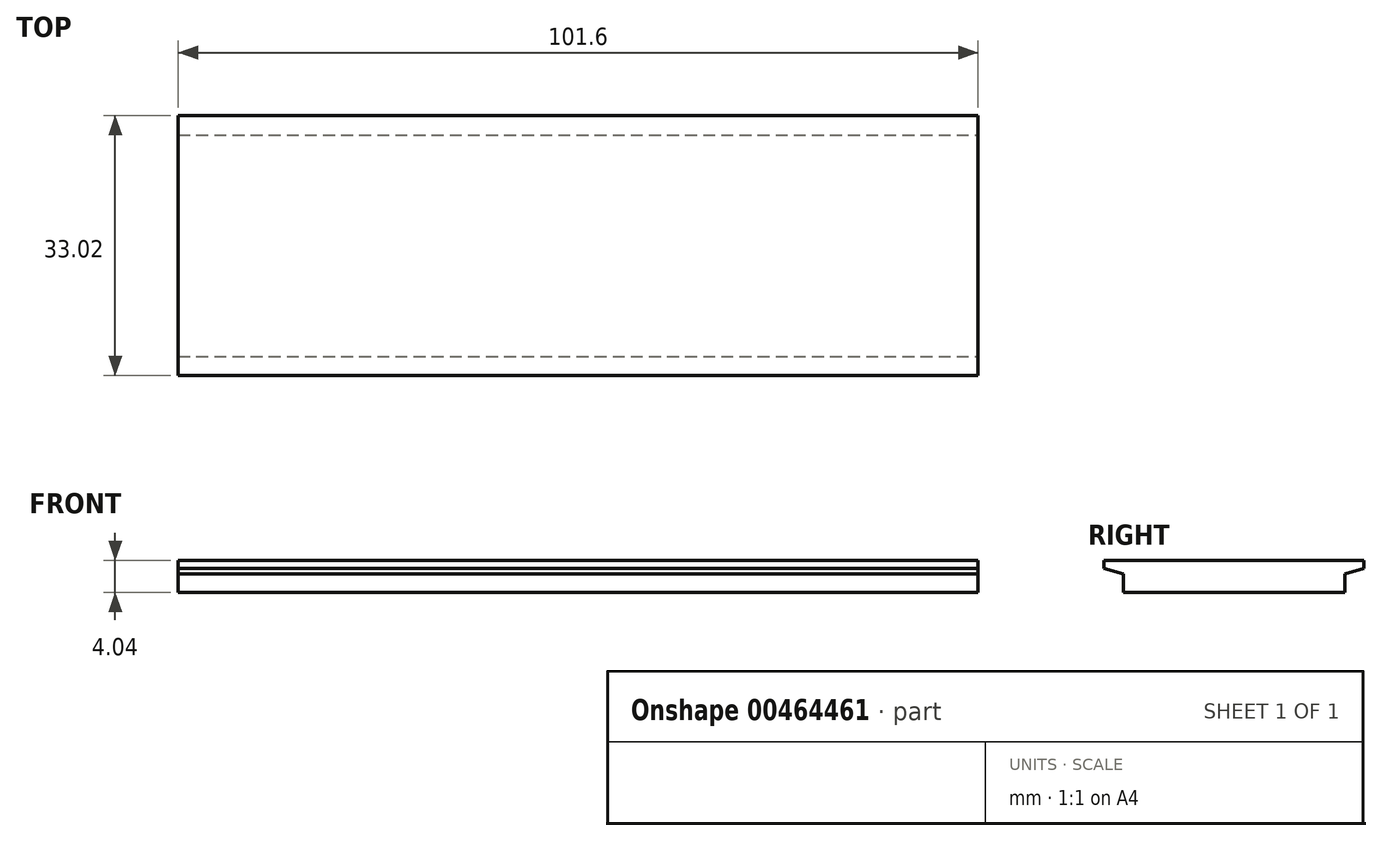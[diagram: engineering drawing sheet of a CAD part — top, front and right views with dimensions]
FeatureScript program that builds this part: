
annotation { "Feature Type Name" : "Feature", "Feature Type Description" : "" }
export const myFeature = defineFeature(function(context is Context, id is Id, definition is map)
    precondition{}
    {
        {
            var Q0;
            Q0=qCreatedBy(makeId("Top.planeOp"),FACE);
            var sketch = newSketch(context, id + "F0", { "sketchPlane" : qUnion([Q0])});
            skLineSegment(sketch, "E0", {"start": v(-50.8, 16.51) * mm, "end": v(50.8, 16.51) * mm});
            skLineSegment(sketch, "E1", {"start": v(50.8, 16.51) * mm, "end": v(50.8, -16.51) * mm});
            skLineSegment(sketch, "E2", {"start": v(50.8, -16.51) * mm, "end": v(-50.8, -16.51) * mm});
            skLineSegment(sketch, "E3", {"start": v(-50.8, -16.51) * mm, "end": v(-50.8, 16.51) * mm});
            skSolve(sketch);
        }
        {
            var Q0;
            Q0=makeQuery(id+"F0.imprint","IMPRINT",FACE,{"disambiguationData":[TD([[makeQuery(id+"F0.imprint","IMPRINT",EDGE,{"derivedFrom":sQuery(id+"F0.wireOp",EDGE,"E0")}),-1.0]])]});
            extrude(context, id + "F1", {"entities" : qUnion([Q0]), "depth" : 4.04 * mm});
        }
        {
            var Q0;
            Q0=makeQuery(id+"F1.opExtrude","SWEPT_FACE",FACE,{"disambiguationData":[OSD([sQuery(id+"F0.wireOp",EDGE,"E1")])]});
            var sketch = newSketch(context, id + "F2", { "sketchPlane" : qUnion([Q0])});
            skLineSegment(sketch, "E4", {"start": v(16.51, 3.02) * mm, "end": v(14.07, 2.33) * mm});
            skLineSegment(sketch, "E5", {"start": v(14.07, 2.33) * mm, "end": v(14.07, 0) * mm});
            skLineSegment(sketch, "E6", {"start": v(16.51, 4.04) * mm, "end": v(16.51, 3.02) * mm});
            skLineSegment(sketch, "E7", {"start": v(0, 0) * mm, "end": v(0, 10.7) * mm, "construction": true});
            skPoint(sketch, "E7.endSnap0", {"position": v(0, 4.04) * mm});
            skLineSegment(sketch, "E8.MirrorCS", {"start": v(-16.51, 4.04) * mm, "end": v(-16.51, 3.02) * mm});
            skLineSegment(sketch, "E9.MirrorCS", {"start": v(-16.51, 3.02) * mm, "end": v(-14.07, 2.33) * mm});
            skLineSegment(sketch, "E10.MirrorCS", {"start": v(-14.07, 2.33) * mm, "end": v(-14.07, 0) * mm});
            skSolve(sketch);
        }
        {
            var Q0;
            {var subQ0=sQuery(id+"F2.wireOp",EDGE,"E9.MirrorCS");Q0=makeQuery(id+"F2.imprint","IMPRINT",FACE,{"disambiguationData":[TD([[makeQuery(id+"F2.imprint","IMPRINT",EDGE,{"derivedFrom":subQ0}),-1.0]])]});}
            var Q1;
            {var subQ0=sQuery(id+"F2.wireOp",EDGE,"E4");Q1=makeQuery(id+"F2.imprint","IMPRINT",FACE,{"disambiguationData":[TD([[makeQuery(id+"F2.imprint","IMPRINT",EDGE,{"derivedFrom":subQ0}),1.0]])]});}
            extrude(context, id + "F3", {"entities" : qUnion([Q0, Q1]), "operationType" : NewBodyOperationType.REMOVE, "oppositeDirection" : true, "depth" : 76.2 * mm});
        }
        {
            var Q0;
            Q0=makeQuery(id+"F3.boolean.opBoolean","COPY",FACE,{"derivedFrom":makeQuery(id+"F3.opExtrude","CAP_FACE",FACE,{"disambiguationData":[OSD([sQuery(id+"F0.wireOp",EDGE,"E1"),sQuery(id+"F0.wireOp",EDGE,"E2"),sQuery(id+"F2.wireOp",EDGE,"E9.MirrorCS"),sQuery(id+"F2.wireOp",EDGE,"E10.MirrorCS")])],"isStart":false})});
            extrude(context, id + "F4", {"entities" : qUnion([Q0]), "operationType" : NewBodyOperationType.REMOVE, "oppositeDirection" : true, "depth" : 38.1 * mm});
        }
        {
            var Q0;
            Q0=makeQuery(id+"F3.boolean.opBoolean","COPY",FACE,{"derivedFrom":makeQuery(id+"F3.opExtrude","CAP_FACE",FACE,{"disambiguationData":[OSD([sQuery(id+"F0.wireOp",EDGE,"E0"),sQuery(id+"F0.wireOp",EDGE,"E1"),sQuery(id+"F2.wireOp",EDGE,"E4"),sQuery(id+"F2.wireOp",EDGE,"E5")])],"isStart":false})});
            extrude(context, id + "F5", {"entities" : qUnion([Q0]), "operationType" : NewBodyOperationType.REMOVE, "oppositeDirection" : true, "depth" : 38.1 * mm});
        }
    });
